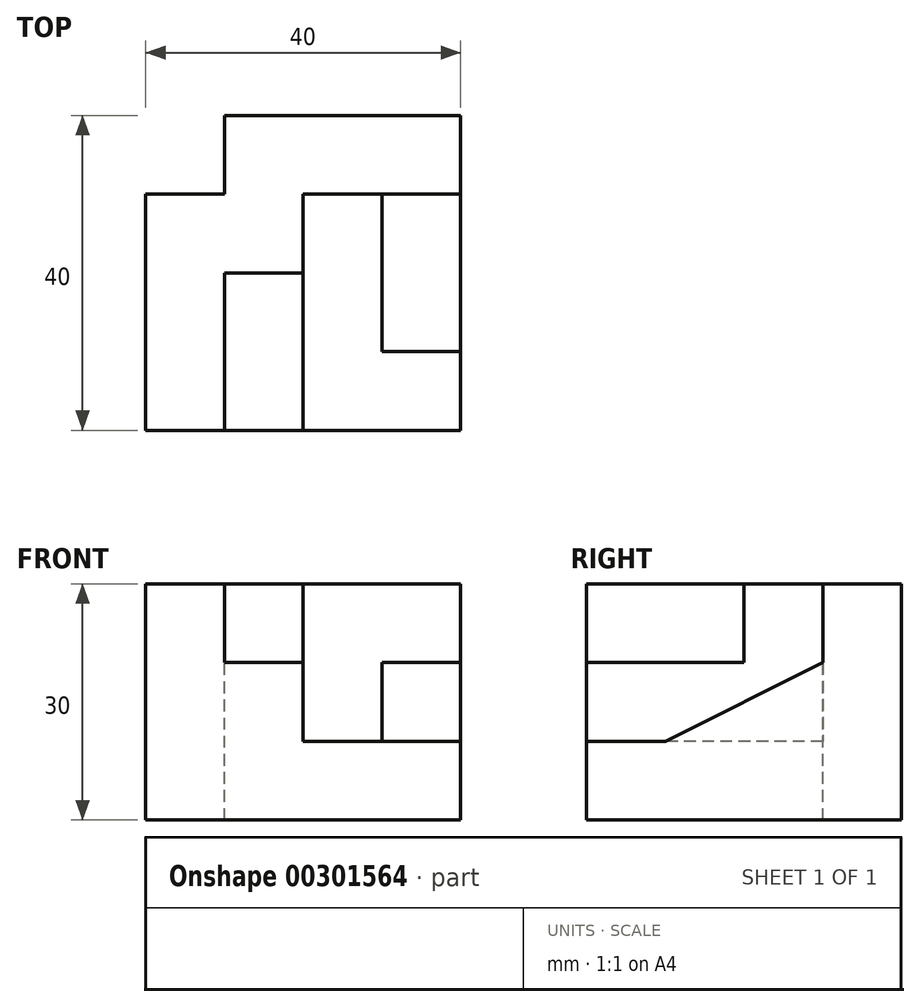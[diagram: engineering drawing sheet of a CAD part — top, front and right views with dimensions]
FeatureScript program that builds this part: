
annotation { "Feature Type Name" : "Feature", "Feature Type Description" : "" }
export const myFeature = defineFeature(function(context is Context, id is Id, definition is map)
    precondition{}
    {
        {
            var Q0;
            Q0=qCreatedBy(makeId("Top.planeOp"),FACE);
            var sketch = newSketch(context, id + "F0", { "sketchPlane" : qUnion([Q0])});
            skLineSegment(sketch, "E0.bottom", {"start": v(-20, 20) * mm, "end": v(20, 20) * mm});
            skLineSegment(sketch, "E0.top", {"start": v(-20, -20) * mm, "end": v(20, -20) * mm});
            skLineSegment(sketch, "E0.left", {"start": v(-20, 20) * mm, "end": v(-20, -20) * mm});
            skLineSegment(sketch, "E0.right", {"start": v(20, 20) * mm, "end": v(20, -20) * mm});
            skPoint(sketch, "E0.middle", {"position": v(0, 0) * mm});
            skSolve(sketch);
        }
        {
            var Q0;
            Q0=makeQuery(id+"F0.imprint","IMPRINT",FACE,{"disambiguationData":[TD([[makeQuery(id+"F0.imprint","IMPRINT",EDGE,{"derivedFrom":sQuery(id+"F0.wireOp",EDGE,"E0.bottom")}),-1.0]])]});
            extrude(context, id + "F1", {"entities" : qUnion([Q0]), "depth" : 30 * mm});
        }
        {
            var Q0;
            Q0=makeQuery(id+"F1.opExtrude","CAP_FACE",FACE,{"disambiguationData":[OSD([sQuery(id+"F0.wireOp",EDGE,"E0.bottom"),sQuery(id+"F0.wireOp",EDGE,"E0.top"),sQuery(id+"F0.wireOp",EDGE,"E0.left"),sQuery(id+"F0.wireOp",EDGE,"E0.right")])],"isStart":false});
            var sketch = newSketch(context, id + "F2", { "sketchPlane" : qUnion([Q0])});
            skLineSegment(sketch, "E1.bottom", {"start": v(-10, 10) * mm, "end": v(-20, 10) * mm});
            skLineSegment(sketch, "E1.top", {"start": v(-10, 20) * mm, "end": v(-20, 20) * mm});
            skLineSegment(sketch, "E1.left", {"start": v(-10, 10) * mm, "end": v(-10, 20) * mm});
            skLineSegment(sketch, "E1.right", {"start": v(-20, 10) * mm, "end": v(-20, 20) * mm});
            skSolve(sketch);
        }
        {
            var Q0;
            Q0=makeQuery(id+"F2.imprint","IMPRINT",FACE,{"disambiguationData":[TD([[makeQuery(id+"F2.imprint","IMPRINT",EDGE,{"derivedFrom":sQuery(id+"F2.wireOp",EDGE,"E1.bottom")}),-1.0]])]});
            extrude(context, id + "F3", {"entities" : qUnion([Q0]), "operationType" : NewBodyOperationType.REMOVE, "oppositeDirection" : true, "depth" : 40 * mm});
        }
        {
            var Q0;
            Q0=makeQuery(id+"F1.opExtrude","SWEPT_FACE",FACE,{"disambiguationData":[OSD([sQuery(id+"F0.wireOp",EDGE,"E0.right")])]});
            var sketch = newSketch(context, id + "F4", { "sketchPlane" : qUnion([Q0])});
            skLineSegment(sketch, "E2", {"start": v(-20, 30) * mm, "end": v(10, 30) * mm});
            skLineSegment(sketch, "E3", {"start": v(10, 30) * mm, "end": v(10, 20) * mm});
            skLineSegment(sketch, "E4", {"start": v(10, 20) * mm, "end": v(-10, 10) * mm});
            skLineSegment(sketch, "E5", {"start": v(-10, 10) * mm, "end": v(-20, 10) * mm});
            skLineSegment(sketch, "E6", {"start": v(-20, 10) * mm, "end": v(-20, 30) * mm});
            skSolve(sketch);
        }
        {
            var Q0;
            Q0=makeQuery(id+"F4.imprint","IMPRINT",FACE,{"disambiguationData":[TD([[makeQuery(id+"F4.imprint","IMPRINT",EDGE,{"derivedFrom":sQuery(id+"F4.wireOp",EDGE,"E2")}),1.0]])]});
            extrude(context, id + "F5", {"entities" : qUnion([Q0]), "operationType" : NewBodyOperationType.REMOVE, "oppositeDirection" : true, "depth" : 20 * mm});
        }
        {
            var Q0;
            Q0=makeQuery(id+"F5.boolean.opBoolean","COPY",FACE,{"derivedFrom":makeQuery(id+"F5.opExtrude","CAP_FACE",FACE,{"disambiguationData":[OSD([sQuery(id+"F4.wireOp",EDGE,"E2"),sQuery(id+"F4.wireOp",EDGE,"E3"),sQuery(id+"F4.wireOp",EDGE,"E4"),sQuery(id+"F4.wireOp",EDGE,"E5"),sQuery(id+"F4.wireOp",EDGE,"E6")])],"isStart":false})});
            var sketch = newSketch(context, id + "F6", { "sketchPlane" : qUnion([Q0])});
            skLineSegment(sketch, "E7.bottom", {"start": v(-20, 30) * mm, "end": v(0, 30) * mm});
            skLineSegment(sketch, "E7.top", {"start": v(-20, 20) * mm, "end": v(0, 20) * mm});
            skLineSegment(sketch, "E7.left", {"start": v(-20, 30) * mm, "end": v(-20, 20) * mm});
            skLineSegment(sketch, "E7.right", {"start": v(0, 30) * mm, "end": v(0, 20) * mm});
            skSolve(sketch);
        }
        {
            var Q0;
            Q0=makeQuery(id+"F6.imprint","IMPRINT",FACE,{"disambiguationData":[TD([[makeQuery(id+"F6.imprint","IMPRINT",EDGE,{"derivedFrom":sQuery(id+"F6.wireOp",EDGE,"E7.bottom")}),1.0]])]});
            extrude(context, id + "F7", {"entities" : qUnion([Q0]), "operationType" : NewBodyOperationType.REMOVE, "oppositeDirection" : true, "depth" : 10 * mm});
        }
        {
            var Q0;
            Q0=makeQuery(id+"F1.opExtrude","SWEPT_FACE",FACE,{"disambiguationData":[OSD([sQuery(id+"F0.wireOp",EDGE,"E0.top")])]});
            var sketch = newSketch(context, id + "F8", { "sketchPlane" : qUnion([Q0])});
            skLineSegment(sketch, "E8.bottom", {"start": v(10, 30) * mm, "end": v(0, 30) * mm});
            skLineSegment(sketch, "E8.top", {"start": v(10, 10) * mm, "end": v(0, 10) * mm});
            skLineSegment(sketch, "E8.left", {"start": v(10, 30) * mm, "end": v(10, 10) * mm});
            skLineSegment(sketch, "E8.right", {"start": v(0, 30) * mm, "end": v(0, 10) * mm});
            skSolve(sketch);
        }
        {
            var Q0;
            {var subQ2=sQuery(id+"F8.wireOp",EDGE,"E8.bottom");Q0=makeQuery(id+"F8.imprint","IMPRINT",FACE,{"disambiguationData":[TD([[makeQuery(id+"F8.imprint","IMPRINT",EDGE,{"derivedFrom":subQ2}),1.0]])]});}
            extrude(context, id + "F9", {"entities" : qUnion([Q0]), "operationType" : NewBodyOperationType.REMOVE, "oppositeDirection" : true, "depth" : 30 * mm});
        }
    });
